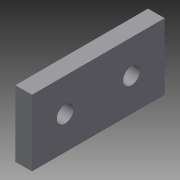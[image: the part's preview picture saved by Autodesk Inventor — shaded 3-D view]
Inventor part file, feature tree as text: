
AUTODESK INVENTOR PART (.ipt)
format: ipt  version: 2015 SP1 (Build 190203100, 203)  size: 79,872 bytes
history: native  units: in
note: dims shown in document units (in); Inventor stores cm internally (conversion verified against a paired STEP export)
features: sketch x2, extrude x1, hole x1
ambient origin geometry x8: Origin, YZ Plane, XZ Plane, XY Plane, X Axis, Y Axis, Z Axis, Center Point
bodies: Solid1 (feature_tree)
feature tree (4):
  extrude  "Extrusion1"  Depth=1.0in
  hole  "Hole1"  [1 undecoded]
  sketch  "Sketch1"  dims[d0=1.0in d1=1.0in]
  sketch  "Sketch2"  dims[d2=0.25in d3=0.0in d6=0.5in d7=0.5in d8=0.25in d9=0.75in d10=0.375in d11=0.25in d12=0.5635in d13=1.0in d14=0.8108in]
note: 1 required parameter value undecoded (feature->parameter linkage not recoverable at this tier; creation-order binding heuristic only, values carry confidence <= 0.55)
